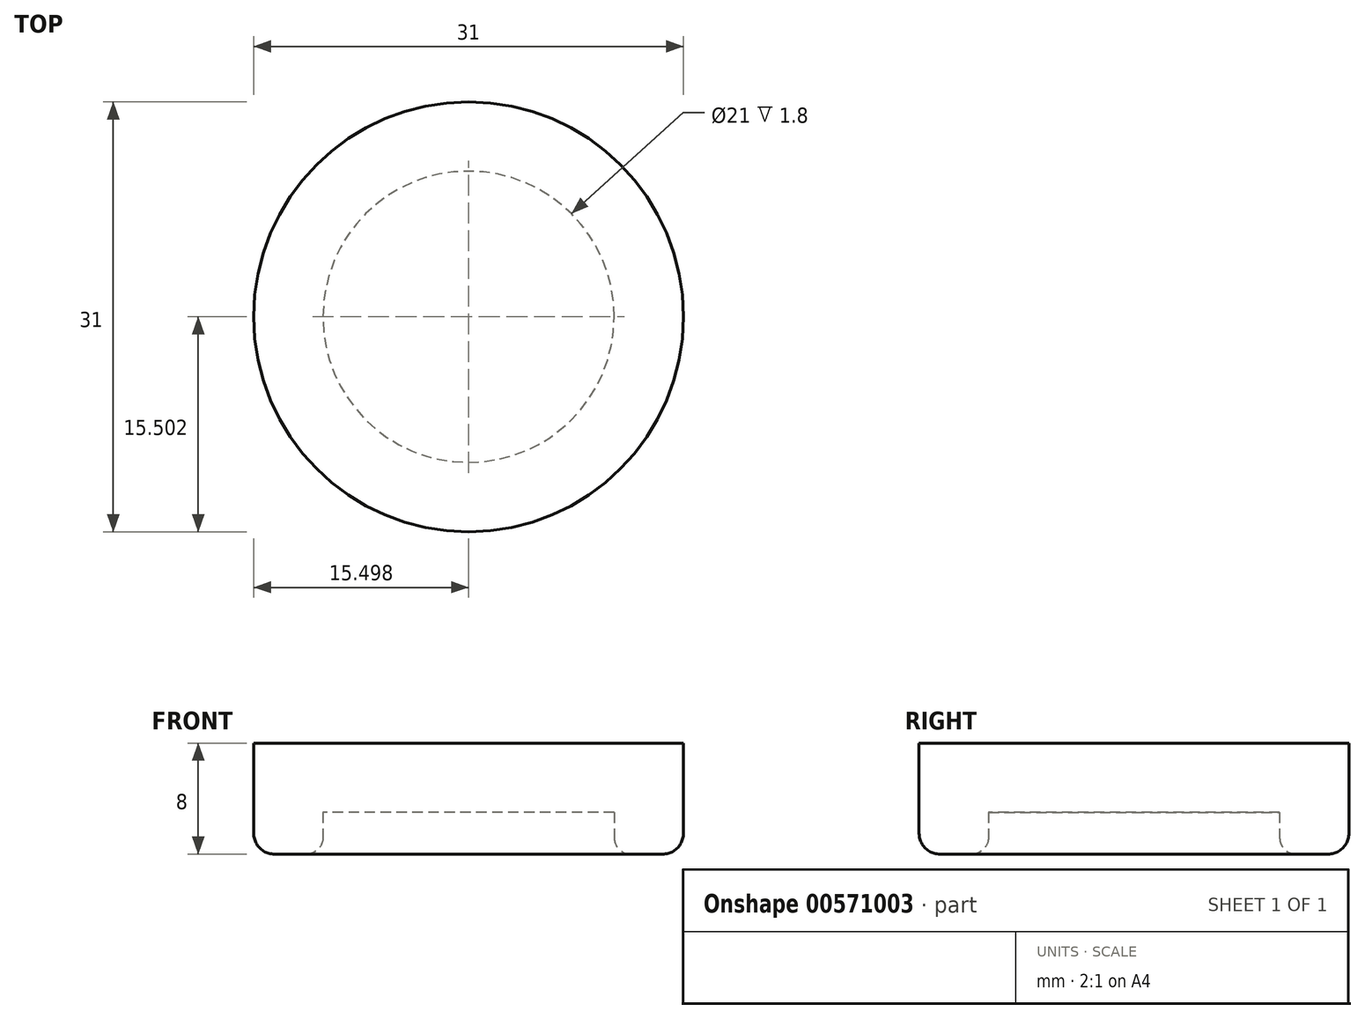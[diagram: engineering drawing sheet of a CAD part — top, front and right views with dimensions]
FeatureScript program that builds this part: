
annotation { "Feature Type Name" : "Feature", "Feature Type Description" : "" }
export const myFeature = defineFeature(function(context is Context, id is Id, definition is map)
    precondition{}
    {
        {
            var Q0;
            Q0=qCreatedBy(makeId("Top.planeOp"),FACE);
            var sketch = newSketch(context, id + "F0", { "sketchPlane" : qUnion([Q0])});
            skCircle(sketch, "E0", {"center": v(-16.12, 8.54) * mm, "radius": 15.5 * mm});
            skSolve(sketch);
        }
        {
            var Q0;
            Q0=makeQuery(id+"F0.imprint","IMPRINT",FACE,{"disambiguationData":[TD([[makeQuery(id+"F0.imprint","IMPRINT",EDGE,{"derivedFrom":sQuery(id+"F0.wireOp",EDGE,"E0")}),1.0]])]});
            extrude(context, id + "F1", {"entities" : qUnion([Q0]), "depth" : 8 * mm, "offsetDistance" : 25 * mm});
        }
        {
            var Q0;
            Q0=makeQuery(id+"F1.opExtrude","CAP_FACE",FACE,{"disambiguationData":[OSD([sQuery(id+"F0.wireOp",EDGE,"E0")])],"isStart":true});
            shell(context, id + "F2", {"entities" : qUnion([Q0]), "thickness" : 5 * mm});
        }
        {
            var Q0;
            Q0=makeQuery(id+"F1.opExtrude","CAP_EDGE",EDGE,{"disambiguationData":[OSD([sQuery(id+"F0.wireOp",EDGE,"E0")])],"isStart":true});
            fillet(context, id + "F3", {"entities" : qUnion([Q0]), "radius" : 1.5 * mm, "tangentPropagation" : true, "allowEdgeOverflow" : false});
        }
        {
            var Q0;
            {var subQ0=sQuery(id+"F0.wireOp",EDGE,"E0");Q0=makeQuery(id+"F2.opShell","OFFSET_EDGE",EDGE,{"disambiguationData":[OSD([subQ0]),TDD([makeQuery(id+"F1.opExtrude","CAP_EDGE",EDGE,{"disambiguationData":[OSD([subQ0])],"isStart":true})])]});}
            var Q1;
            Q1=makeQuery(id+"F3.opFillet","BLEND_FACE",FACE,{"disambiguationData":[OSD([sQuery(id+"F0.wireOp",EDGE,"E0")])]});
            fillet(context, id + "F4", {"entities" : qUnion([Q0, Q1]), "radius" : 1.2 * mm, "tangentPropagation" : true, "allowEdgeOverflow" : false});
        }
    });
